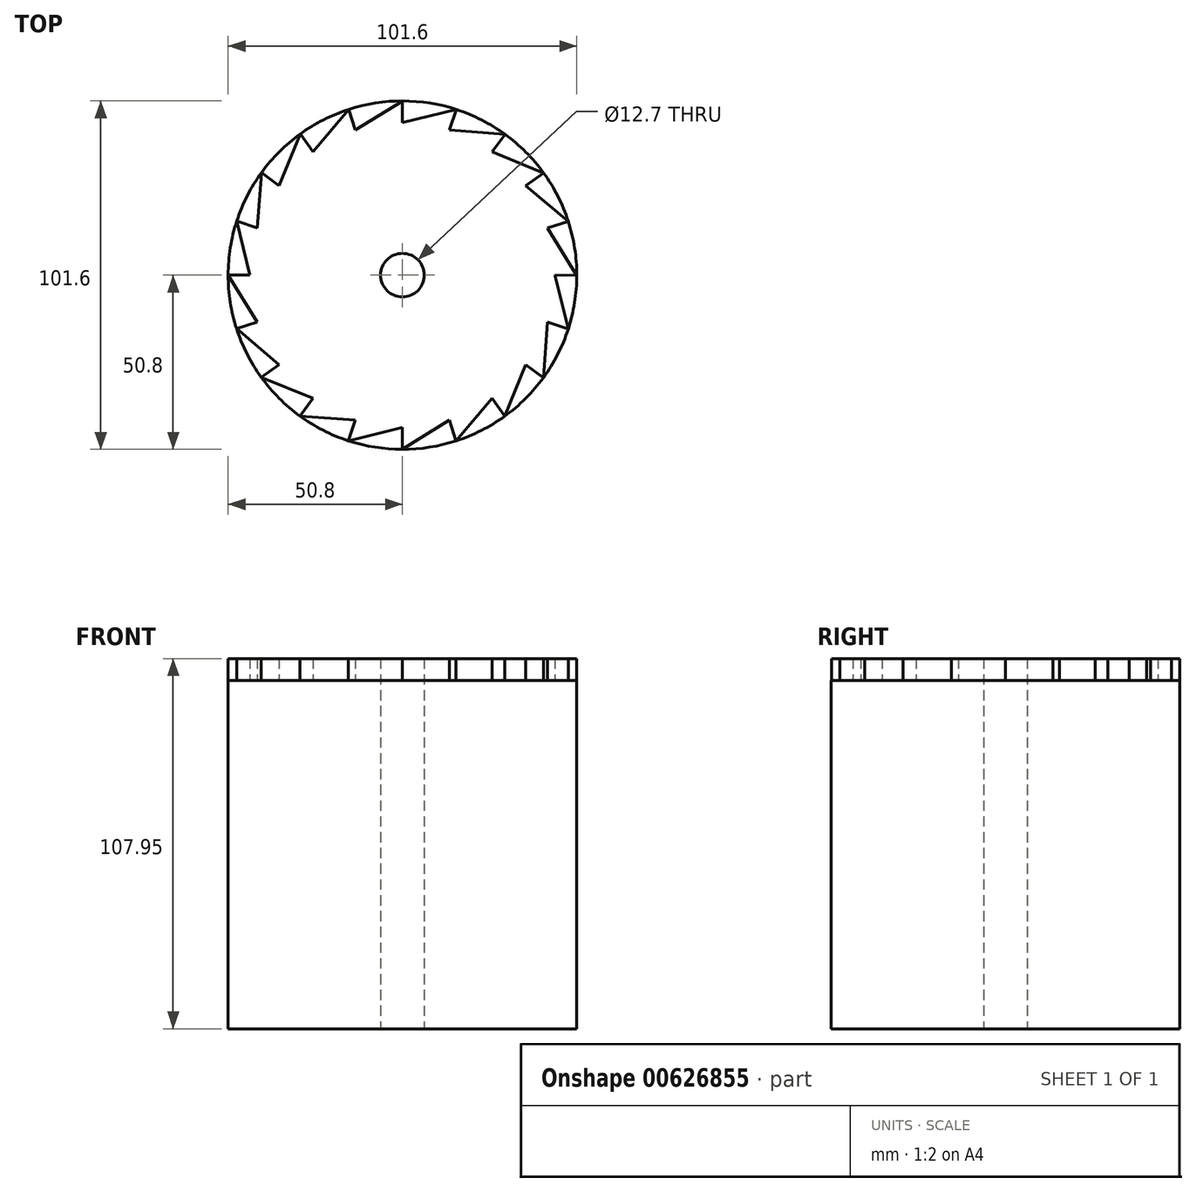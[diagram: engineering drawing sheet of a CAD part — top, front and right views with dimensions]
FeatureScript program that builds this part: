
annotation { "Feature Type Name" : "Feature", "Feature Type Description" : "" }
export const myFeature = defineFeature(function(context is Context, id is Id, definition is map)
    precondition{}
    {
        {
            var Q0;
            Q0=qCreatedBy(makeId("Top.planeOp"),FACE);
            var sketch = newSketch(context, id + "F0", { "sketchPlane" : qUnion([Q0])});
            skCircle(sketch, "E0", {"center": v(0, 0) * mm, "radius": 50.8 * mm});
            skLineSegment(sketch, "E1", {"start": v(0, 50.8) * mm, "end": v(0, 44.45) * mm});
            skLineSegment(sketch, "E2", {"start": v(0, 44.45) * mm, "end": v(15.76, 48.3) * mm});
            skLineSegment(sketch, "E3", {"start": v(0, 50.8) * mm, "end": v(0, -50.8) * mm, "construction": true});
            skLineSegment(sketch, "E4.1.0", {"start": v(-13.74, 42.27) * mm, "end": v(0.07, 50.8) * mm});
            skLineSegment(sketch, "E4.2.0", {"start": v(-26.13, 35.96) * mm, "end": v(-15.63, 48.33) * mm});
            skLineSegment(sketch, "E4.3.0", {"start": v(-35.96, 26.13) * mm, "end": v(-29.8, 41.14) * mm});
            skLineSegment(sketch, "E4.4.0", {"start": v(-42.27, 13.74) * mm, "end": v(-41.06, 29.91) * mm});
            skLineSegment(sketch, "E4.5.0", {"start": v(-44.45, 0) * mm, "end": v(-48.3, 15.76) * mm});
            skLineSegment(sketch, "E4.6.0", {"start": v(-42.27, -13.74) * mm, "end": v(-50.8, 0.07) * mm});
            skLineSegment(sketch, "E4.7.0", {"start": v(-35.96, -26.13) * mm, "end": v(-48.33, -15.63) * mm});
            skLineSegment(sketch, "E4.8.0", {"start": v(-26.13, -35.96) * mm, "end": v(-41.14, -29.8) * mm});
            skLineSegment(sketch, "E4.9.0", {"start": v(-13.74, -42.27) * mm, "end": v(-29.91, -41.06) * mm});
            skLineSegment(sketch, "E4.10.0", {"start": v(0, -44.45) * mm, "end": v(-15.76, -48.3) * mm});
            skLineSegment(sketch, "E4.11.0", {"start": v(13.74, -42.27) * mm, "end": v(-0.07, -50.8) * mm});
            skLineSegment(sketch, "E4.12.0", {"start": v(26.13, -35.96) * mm, "end": v(15.63, -48.33) * mm});
            skLineSegment(sketch, "E4.13.0", {"start": v(35.96, -26.13) * mm, "end": v(29.8, -41.14) * mm});
            skLineSegment(sketch, "E4.14.0", {"start": v(42.27, -13.74) * mm, "end": v(41.06, -29.91) * mm});
            skLineSegment(sketch, "E4.15.0", {"start": v(44.45, 0) * mm, "end": v(48.3, -15.76) * mm});
            skLineSegment(sketch, "E4.16.0", {"start": v(42.27, 13.74) * mm, "end": v(50.8, -0.07) * mm});
            skLineSegment(sketch, "E4.17.0", {"start": v(35.96, 26.13) * mm, "end": v(48.33, 15.63) * mm});
            skLineSegment(sketch, "E4.18.0", {"start": v(26.13, 35.96) * mm, "end": v(41.14, 29.8) * mm});
            skLineSegment(sketch, "E4.19.0", {"start": v(13.74, 42.27) * mm, "end": v(29.91, 41.06) * mm});
            skLineSegment(sketch, "E5", {"start": v(15.76, 48.3) * mm, "end": v(13.74, 42.27) * mm});
            skLineSegment(sketch, "E6", {"start": v(26.13, 35.96) * mm, "end": v(29.91, 41.06) * mm});
            skLineSegment(sketch, "E7", {"start": v(35.96, 26.13) * mm, "end": v(41.14, 29.8) * mm});
            skLineSegment(sketch, "E8", {"start": v(42.27, 13.74) * mm, "end": v(48.33, 15.63) * mm});
            skLineSegment(sketch, "E9", {"start": v(44.45, 0) * mm, "end": v(50.8, -0.07) * mm});
            skLineSegment(sketch, "E10", {"start": v(42.27, -13.74) * mm, "end": v(48.3, -15.76) * mm});
            skLineSegment(sketch, "E11", {"start": v(35.96, -26.13) * mm, "end": v(41.06, -29.91) * mm});
            skLineSegment(sketch, "E12", {"start": v(26.13, -35.96) * mm, "end": v(29.8, -41.14) * mm});
            skLineSegment(sketch, "E13", {"start": v(13.74, -42.27) * mm, "end": v(15.63, -48.33) * mm});
            skLineSegment(sketch, "E14", {"start": v(0, -44.45) * mm, "end": v(0, -50.8) * mm});
            skLineSegment(sketch, "E15", {"start": v(-13.74, -42.27) * mm, "end": v(-15.76, -48.3) * mm});
            skLineSegment(sketch, "E16", {"start": v(-26.13, -35.96) * mm, "end": v(-29.91, -41.06) * mm});
            skLineSegment(sketch, "E17", {"start": v(-35.96, -26.13) * mm, "end": v(-41.14, -29.8) * mm});
            skLineSegment(sketch, "E18", {"start": v(-42.27, -13.74) * mm, "end": v(-48.33, -15.63) * mm});
            skLineSegment(sketch, "E19", {"start": v(-44.45, 0) * mm, "end": v(-50.8, 0.07) * mm});
            skLineSegment(sketch, "E20", {"start": v(-42.27, 13.74) * mm, "end": v(-48.3, 15.76) * mm});
            skLineSegment(sketch, "E21", {"start": v(-35.96, 26.13) * mm, "end": v(-41.06, 29.91) * mm});
            skLineSegment(sketch, "E22", {"start": v(-26.13, 35.96) * mm, "end": v(-29.8, 41.14) * mm});
            skLineSegment(sketch, "E23", {"start": v(-13.74, 42.27) * mm, "end": v(-15.63, 48.33) * mm});
            skCircle(sketch, "E24", {"center": v(0, 0) * mm, "radius": 6.35 * mm});
            skSolve(sketch);
        }
        {
            var Q0;
            {var subQ9=sQuery(id+"F0.wireOp",EDGE,"E2");Q0=makeQuery(id+"F0.imprint","IMPRINT",FACE,{"disambiguationData":[TD([[makeQuery(id+"F0.imprint","IMPRINT",EDGE,{"derivedFrom":subQ9}),-1.0]])]});}
            extrude(context, id + "F1", {"entities" : qUnion([Q0]), "depth" : 107.95 * mm, "offsetDistance" : 25.4 * mm});
        }
        {
            var Q0;
            Q0 = qSketchRegion(id + "F0", true);
            extrude(context, id + "F2", {"entities" : qUnion([Q0]), "operationType" : NewBodyOperationType.ADD, "depth" : 101.6 * mm, "offsetDistance" : 25.4 * mm});
        }
    });
